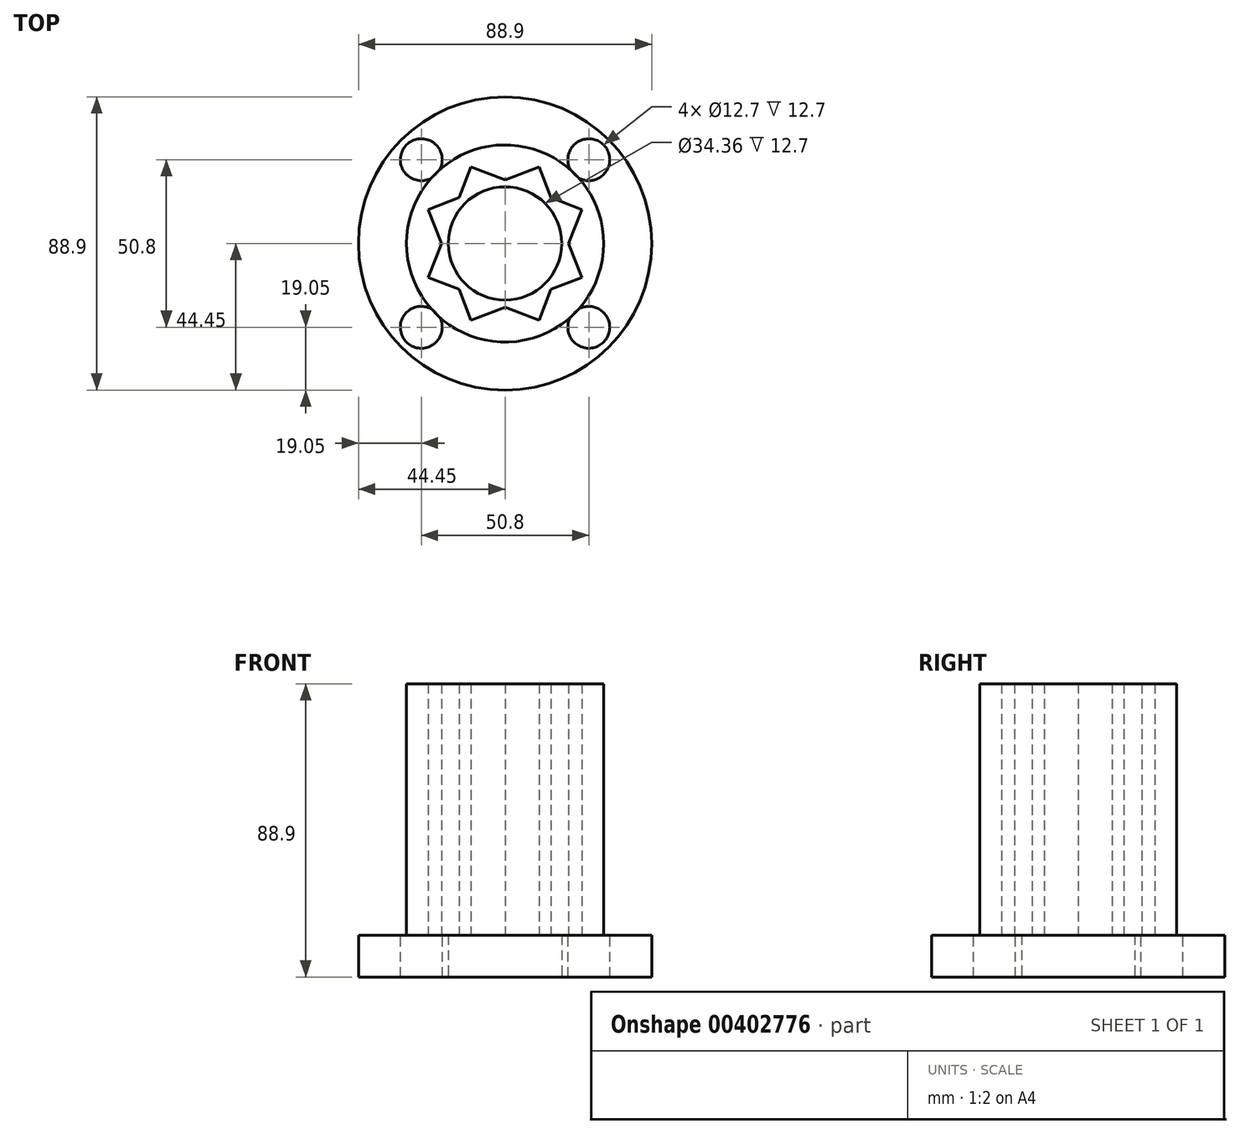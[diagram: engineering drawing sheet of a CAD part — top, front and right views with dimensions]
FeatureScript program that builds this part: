
annotation { "Feature Type Name" : "Feature", "Feature Type Description" : "" }
export const myFeature = defineFeature(function(context is Context, id is Id, definition is map)
    precondition{}
    {
        {
            var Q0;
            Q0=qCreatedBy(makeId("Top.planeOp"),FACE);
            var sketch = newSketch(context, id + "F0", { "sketchPlane" : qUnion([Q0])});
            skCircle(sketch, "E0", {"center": v(0, 0) * mm, "radius": 29.88 * mm});
            skCircle(sketch, "E1", {"center": v(0, 0) * mm, "radius": 17.18 * mm});
            skSolve(sketch);
        }
        {
            var Q0;
            Q0=makeQuery(id+"F0.imprint","IMPRINT",FACE,{"disambiguationData":[TD([[makeQuery(id+"F0.imprint","IMPRINT",EDGE,{"derivedFrom":sQuery(id+"F0.wireOp",EDGE,"E0")}),1.0]])]});
            extrude(context, id + "F1", {"entities" : qUnion([Q0]), "depth" : 76.2 * mm});
        }
        {
            var Q0;
            Q0=qCreatedBy(makeId("Top.planeOp"),FACE);
            var sketch = newSketch(context, id + "F2", { "sketchPlane" : qUnion([Q0])});
            skCircle(sketch, "E2", {"center": v(0, 0) * mm, "radius": 17.18 * mm});
            skCircle(sketch, "E3", {"center": v(0, 0) * mm, "radius": 44.45 * mm});
            skSolve(sketch);
        }
        {
            var Q0;
            Q0=makeQuery(id+"F2.imprint","IMPRINT",FACE,{"disambiguationData":[TD([[makeQuery(id+"F2.imprint","IMPRINT",EDGE,{"derivedFrom":sQuery(id+"F2.wireOp",EDGE,"E2")}),-1.0]])]});
            extrude(context, id + "F3", {"entities" : qUnion([Q0]), "operationType" : NewBodyOperationType.ADD, "oppositeDirection" : true, "depth" : 12.7 * mm});
        }
        {
            var Q0;
            Q0=qCreatedBy(makeId("Top.planeOp"),FACE);
            var sketch = newSketch(context, id + "F4", { "sketchPlane" : qUnion([Q0])});
            skCircle(sketch, "E4.cCircle", {"center": v(0, 0) * mm, "radius": 18 * mm, "construction": true});
            skLineSegment(sketch, "E4.0", {"start": v(10.3, 23.28) * mm, "end": v(23.28, -10.3) * mm});
            skLineSegment(sketch, "E4.1", {"start": v(23.28, -10.3) * mm, "end": v(-10.3, -23.28) * mm});
            skLineSegment(sketch, "E4.2", {"start": v(-10.3, -23.28) * mm, "end": v(-23.28, 10.3) * mm});
            skLineSegment(sketch, "E4.3", {"start": v(-23.28, 10.3) * mm, "end": v(10.3, 23.28) * mm});
            skPoint(sketch, "E4.0.midPoint", {"position": v(16.8, 6.49) * mm});
            skLineSegment(sketch, "E5.0", {"start": v(-23.28, -10.3) * mm, "end": v(-10.3, 23.28) * mm});
            skLineSegment(sketch, "E5.1", {"start": v(-10.3, 23.28) * mm, "end": v(23.28, 10.3) * mm});
            skLineSegment(sketch, "E5.2", {"start": v(23.28, 10.3) * mm, "end": v(10.3, -23.28) * mm});
            skLineSegment(sketch, "E5.3", {"start": v(10.3, -23.28) * mm, "end": v(-23.28, -10.3) * mm});
            skPoint(sketch, "E5.0.midPoint", {"position": v(-16.8, 6.49) * mm});
            skSolve(sketch);
        }
        {
            var Q0;
            Q0 = qSketchRegion(id + "F4", true);
            extrude(context, id + "F5", {"entities" : qUnion([Q0]), "operationType" : NewBodyOperationType.REMOVE, "depth" : 444 * mm});
        }
        {
            var Q0;
            Q0=qCreatedBy(makeId("Top.planeOp"),FACE);
            var sketch = newSketch(context, id + "F6", { "sketchPlane" : qUnion([Q0])});
            skLineSegment(sketch, "E6.bottom", {"start": v(25.4, -25.4) * mm, "end": v(-25.4, -25.4) * mm});
            skLineSegment(sketch, "E6.top", {"start": v(25.4, 25.4) * mm, "end": v(-25.4, 25.4) * mm});
            skLineSegment(sketch, "E6.left", {"start": v(25.4, -25.4) * mm, "end": v(25.4, 25.4) * mm});
            skLineSegment(sketch, "E6.right", {"start": v(-25.4, -25.4) * mm, "end": v(-25.4, 25.4) * mm});
            skPoint(sketch, "E6.middle", {"position": v(0, 0) * mm});
            skSolve(sketch);
        }
        {
            var Q0;
            Q0=qCreatedBy(makeId("Top.planeOp"),FACE);
            var sketch = newSketch(context, id + "F7", { "sketchPlane" : qUnion([Q0])});
            skCircle(sketch, "E7", {"center": v(-25.4, -25.4) * mm, "radius": 6.35 * mm});
            skCircle(sketch, "E8", {"center": v(25.4, -25.4) * mm, "radius": 6.35 * mm});
            skCircle(sketch, "E9", {"center": v(25.4, 25.4) * mm, "radius": 6.35 * mm});
            skCircle(sketch, "E10", {"center": v(-25.4, 25.4) * mm, "radius": 6.35 * mm});
            skSolve(sketch);
        }
        {
            var Q0;
            Q0 = qSketchRegion(id + "F7", true);
            extrude(context, id + "F8", {"entities" : qUnion([Q0]), "operationType" : NewBodyOperationType.REMOVE, "oppositeDirection" : true, "depth" : 25.4 * mm});
        }
    });
